# Revit family: Deca_Bacia Sanitária Wish_P.280_Caixa Acoplada
name_source: partatom
category: Plumbing Fixtures
revit_build: Autodesk Revit Architecture 2012 (Build: 20120126_0600(x64)
units: mm (PartAtom-declared; Revit-internal decimal feet)

## types (2) — shared parameters
Acompanha o Produto = Fixação
Aprovado por = Contino/quattroD
Assembly Code = D2010110
Atendimento ao Cliente = 0800-011-7073
Consumo = 6 lpf
Criado por = Contino/quattroD
Description = Bacia sanitária com caixa acoplada
Diâmetro Ponto de Esgoto = 100 mm  [stored 0.328084 ft]
Diâmetro Água Fria = 15 mm  [stored 0.0492126 ft]
Flow Pressure = 0.00 psi
Linha = Wish
Louça/Metais = Louça
Manufacturer = Deca
Material = Deca_Vitreous China
Norma = ABNT NBR 15097-1:2011
Peso Liquido (Kg) = 34.7
Produto = Bacia sanitária para caixa acoplada Wish
Raio Ponto de Esgoto = 50 mm  [stored 0.164042 ft]
Raio Água Fria = 8 mm  [stored 0.0262467 ft]
Segmento = Luxo
URL = www.deca.com.br/produtos
Variações de COR = Branco (P.280.17); Ébano (P.280.95).
Vendido Separadamente = Anel de vedação: (AV.90.01 ); Ligação Flexível: Cromado: 30 cm (4607.C.030), 40 cm (4607.C.040), 50 cm (4607.C.050).  Assentos Compatíveis: Assento termofixo low close e easy clean:  Branco (AP.286.17), Ébano (AP.286.95).  Assento Poliéster slow slose - Fixação Cromada e Dourada: Branco (AP.287.17), Ébano (AP.287.95).
zero-valued in all types: CWFU, Default Elevation, WFU

## per-type parameters (varying)
| type | Bacia | Caixa - Family | Código | Model |
| P.280.17_Branco Gelo GE17 | Deca GE17 Branco Gelo Cerâmica | Deca_Shared_Caixa Acoplada para Bacia_P.280 : CD.28F.17_Branco Gelo GE17_Dual Flux 3lpf/6lpf | P.280.17 | P.280.17 |
| P.280.95_Ébano EB95 | Deca EB95 Ébano Cerâmica | Deca_Shared_Caixa Acoplada para Bacia_P.280 : CD.28F.95_Ébano EB95_Dual Flux 3lpf/6lpf | P.280.95 | P.280.95 |

note: [stored X ft] marks values corroborated as IEEE doubles in the binary element streams (Revit-internal decimal feet)

## geometry (parser evidence)
native form markers: Blend x16, Sweep x2
no freeform markers — native parametric forms only
